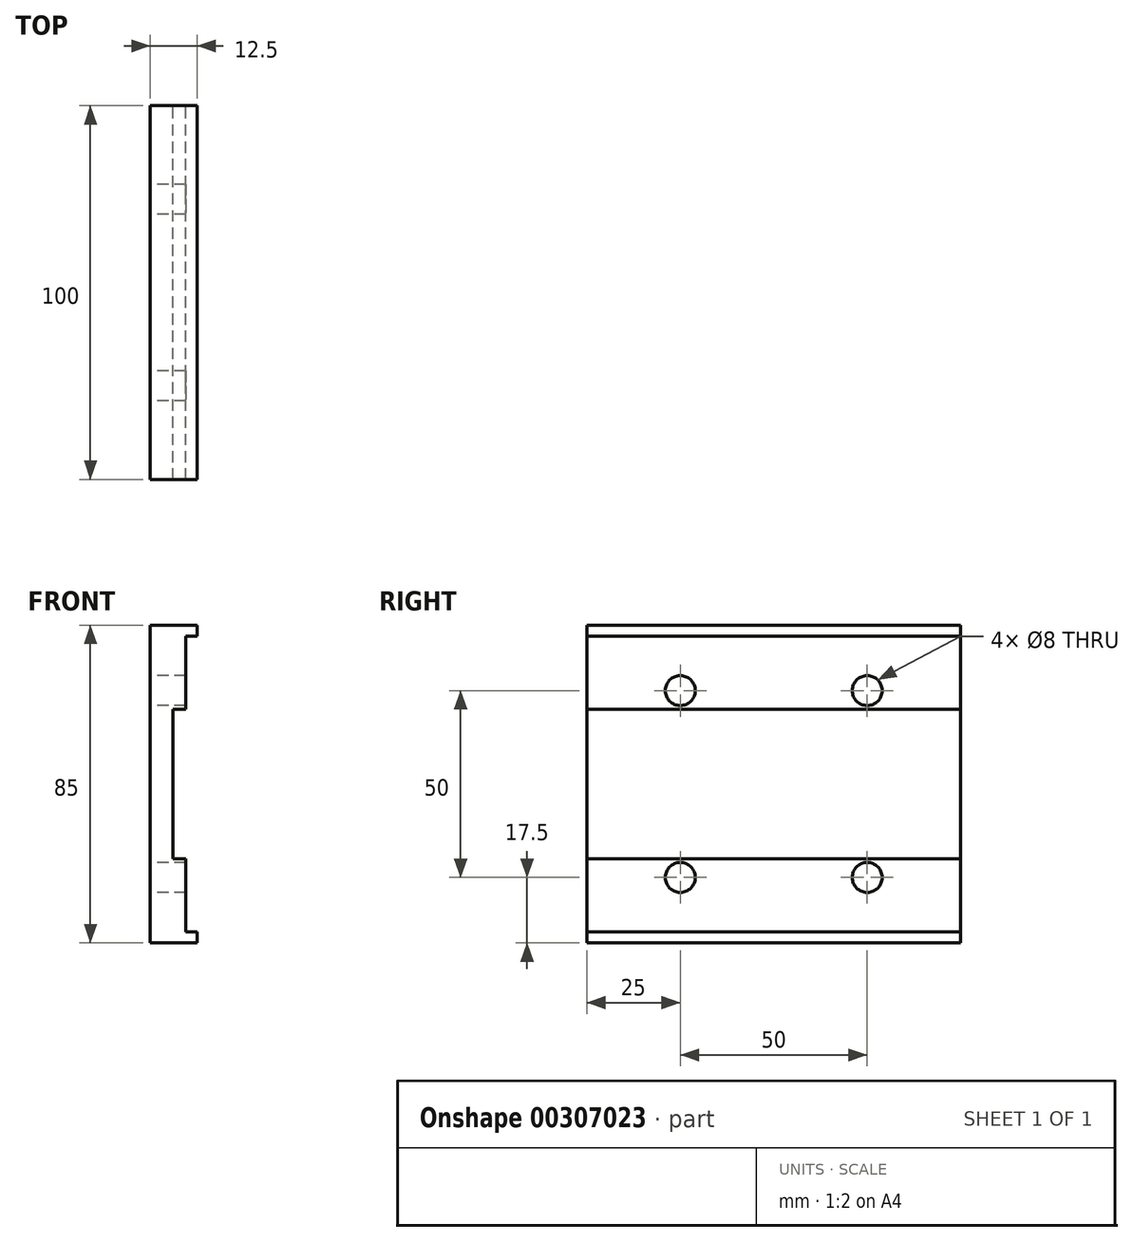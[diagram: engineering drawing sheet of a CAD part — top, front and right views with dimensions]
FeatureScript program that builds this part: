
annotation { "Feature Type Name" : "Feature", "Feature Type Description" : "" }
export const myFeature = defineFeature(function(context is Context, id is Id, definition is map)
    precondition{}
    {
        {
            var Q0;
            Q0=qCreatedBy(makeId("Front.planeOp"),FACE);
            var sketch = newSketch(context, id + "F0", { "sketchPlane" : qUnion([Q0])});
            skLineSegment(sketch, "E0", {"start": v(-19.05, 42.5) * mm, "end": v(-6.55, 42.5) * mm});
            skLineSegment(sketch, "E1", {"start": v(-6.55, 42.5) * mm, "end": v(-6.55, 39.5) * mm});
            skLineSegment(sketch, "E2", {"start": v(-6.55, 39.5) * mm, "end": v(-9.55, 39.5) * mm});
            skLineSegment(sketch, "E3", {"start": v(-9.55, 39.5) * mm, "end": v(-9.55, 20) * mm});
            skLineSegment(sketch, "E4", {"start": v(-9.55, 20) * mm, "end": v(-13.05, 20) * mm});
            skLineSegment(sketch, "E5", {"start": v(-13.05, 20) * mm, "end": v(-13.05, 0) * mm});
            skLineSegment(sketch, "E6", {"start": v(-19.05, 0) * mm, "end": v(-19.05, 42.5) * mm});
            skLineSegment(sketch, "E7.MirrorCS", {"start": v(-9.55, -20) * mm, "end": v(-13.05, -20) * mm});
            skLineSegment(sketch, "E8.MirrorCS", {"start": v(-6.55, -42.5) * mm, "end": v(-6.55, -39.5) * mm});
            skLineSegment(sketch, "E9.MirrorCS", {"start": v(-19.05, -42.5) * mm, "end": v(-6.55, -42.5) * mm});
            skLineSegment(sketch, "E10.MirrorCS", {"start": v(-6.55, -39.5) * mm, "end": v(-9.55, -39.5) * mm});
            skLineSegment(sketch, "E11.MirrorCS", {"start": v(-9.55, -39.5) * mm, "end": v(-9.55, -20) * mm});
            skLineSegment(sketch, "E12.MirrorCS", {"start": v(-13.05, -20) * mm, "end": v(-13.05, 0) * mm});
            skLineSegment(sketch, "E13.MirrorCS", {"start": v(-19.05, 0) * mm, "end": v(-19.05, -42.5) * mm});
            skSolve(sketch);
        }
        {
            var Q0;
            Q0=qSketchRegion(id+"F0",true);
            extrude(context, id + "F1", {"entities" : qUnion([Q0]), "depth" : 100 * mm});
        }
        {
            var Q0;
            Q0=makeQuery(id+"F1.opExtrude","SWEPT_FACE",FACE,{"disambiguationData":[OSD([sQuery(id+"F0.wireOp",EDGE,"E6"),sQuery(id+"F0.wireOp",EDGE,"E13.MirrorCS")])]});
            var sketch = newSketch(context, id + "F2", { "sketchPlane" : qUnion([Q0])});
            skCircle(sketch, "E14", {"center": v(25, 25) * mm, "radius": 4 * mm});
            skCircle(sketch, "E15", {"center": v(75, 25) * mm, "radius": 4 * mm});
            skCircle(sketch, "E16.MirrorC", {"center": v(25, -25) * mm, "radius": 4 * mm});
            skCircle(sketch, "E17.MirrorC", {"center": v(75, -25) * mm, "radius": 4 * mm});
            skSolve(sketch);
        }
        {
            var Q0;
            Q0=qSketchRegion(id+"F2",true);
            extrude(context, id + "F3", {"entities" : qUnion([Q0]), "operationType" : NewBodyOperationType.REMOVE, "oppositeDirection" : true, "depth" : 25 * mm});
        }
    });
